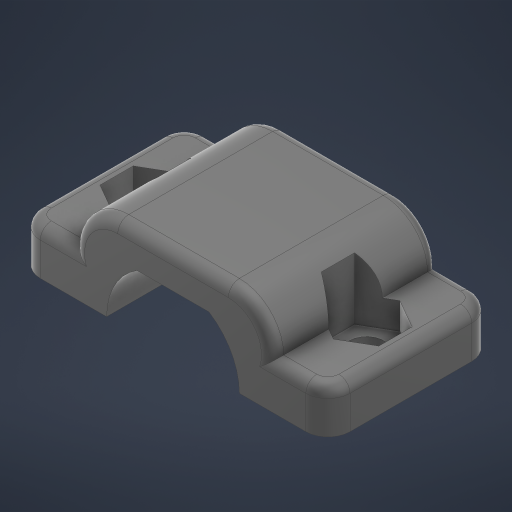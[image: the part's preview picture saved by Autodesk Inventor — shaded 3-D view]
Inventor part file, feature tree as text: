
AUTODESK INVENTOR PART (.ipt)
format: ipt  version: 2024 (Build 280153000, 153)  size: 336,384 bytes
history: native  units: in
note: dims shown in document units (in); Inventor stores cm internally (conversion verified against a paired STEP export)
features: sketch x3, extrude x2, plane x2, fillet x2, hole x1, mirror x1
ambient origin geometry x8: Origin, YZ Plane, XZ Plane, XY Plane, X Axis, Y Axis, Z Axis, Center Point
bodies: Solid1 (feature_tree)
feature tree (11):
  extrude  "Extrusion2"  Depth=0.1181in TaperAngle=0.0deg
  plane  "Work Plane1"
  extrude  "Extrusion3"  Depth=0.1575in
  hole  "Hole1"  [1 undecoded]
  mirror  "Mirror1"
  plane  "Work Plane2"
  fillet  "Fillet3"  Radius=0.2953in
  fillet  "Fillet4"  Radius=0.0787in
  sketch  "Sketch3"  dims[d20=0.1575in d21=0.1969in d22=0.315in d23=0.1181in d24=0.5906in d25=0.0in]
  sketch  "Sketch4"  dims[d26=0.2366in d27=0.1575in]
  sketch  "Sketch5"  dims[d28=0.315in d29=0.0945in d30=0.0in d31=0.0in d32=0.122in d33=0.2362in d34=0.1575in d35=0.0787in d36=90.0deg d37=0.315in d38=0.8108in d39=0.2953in d40=0.2953in d42=0.0787in d43=0.0394in]
note: 1 required parameter value undecoded (feature->parameter linkage not recoverable at this tier; creation-order binding heuristic only, values carry confidence <= 0.55)
